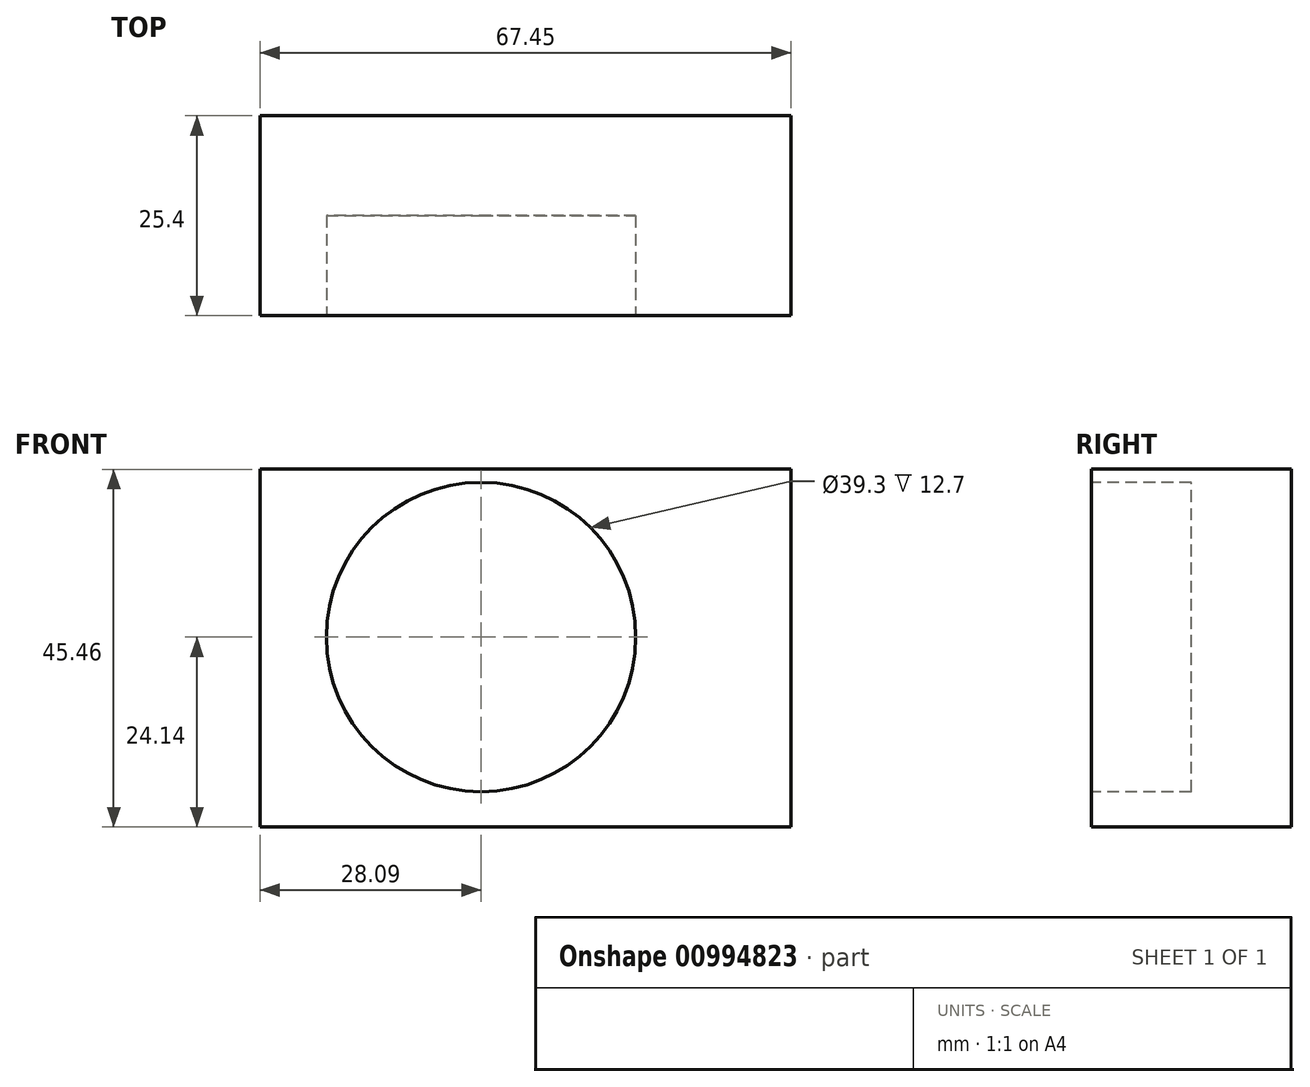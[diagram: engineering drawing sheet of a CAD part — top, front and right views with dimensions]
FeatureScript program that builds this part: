
annotation { "Feature Type Name" : "Feature", "Feature Type Description" : "" }
export const myFeature = defineFeature(function(context is Context, id is Id, definition is map)
    precondition{}
    {
        {
            var Q0;
            Q0=qCreatedBy(makeId("Front.planeOp"),FACE);
            var sketch = newSketch(context, id + "F0", { "sketchPlane" : qUnion([Q0])});
            skLineSegment(sketch, "E0.bottom", {"start": v(-28.09, 21.32) * mm, "end": v(39.36, 21.32) * mm});
            skLineSegment(sketch, "E0.top", {"start": v(-28.09, -24.14) * mm, "end": v(39.36, -24.14) * mm});
            skLineSegment(sketch, "E0.left", {"start": v(-28.09, 21.32) * mm, "end": v(-28.09, -24.14) * mm});
            skLineSegment(sketch, "E0.right", {"start": v(39.36, 21.32) * mm, "end": v(39.36, -24.14) * mm});
            skSolve(sketch);
        }
        {
            var Q0;
            Q0=makeQuery(id+"F0.imprint","IMPRINT",FACE,{"disambiguationData":[TD([[makeQuery(id+"F0.imprint","IMPRINT",EDGE,{"derivedFrom":sQuery(id+"F0.wireOp",EDGE,"E0.bottom")}),-1.0]])]});
            extrude(context, id + "F1", {"entities" : qUnion([Q0]), "depth" : 25.4 * mm, "offsetDistance" : 25.4 * mm});
        }
        {
            var Q0;
            Q0=makeQuery(id+"F1.opExtrude","CAP_FACE",FACE,{"disambiguationData":[OSD([sQuery(id+"F0.wireOp",EDGE,"E0.bottom"),sQuery(id+"F0.wireOp",EDGE,"E0.top"),sQuery(id+"F0.wireOp",EDGE,"E0.left"),sQuery(id+"F0.wireOp",EDGE,"E0.right")])],"isStart":false});
            var sketch = newSketch(context, id + "F2", { "sketchPlane" : qUnion([Q0])});
            skCircle(sketch, "E1", {"center": v(0, 0) * mm, "radius": 19.65 * mm});
            skSolve(sketch);
        }
        {
            var Q0;
            Q0 = qSketchRegion(id + "F2", true);
            extrude(context, id + "F3", {"entities" : qUnion([Q0]), "operationType" : NewBodyOperationType.REMOVE, "depth" : -12.7 * mm, "offsetDistance" : 25.4 * mm});
        }
    });
